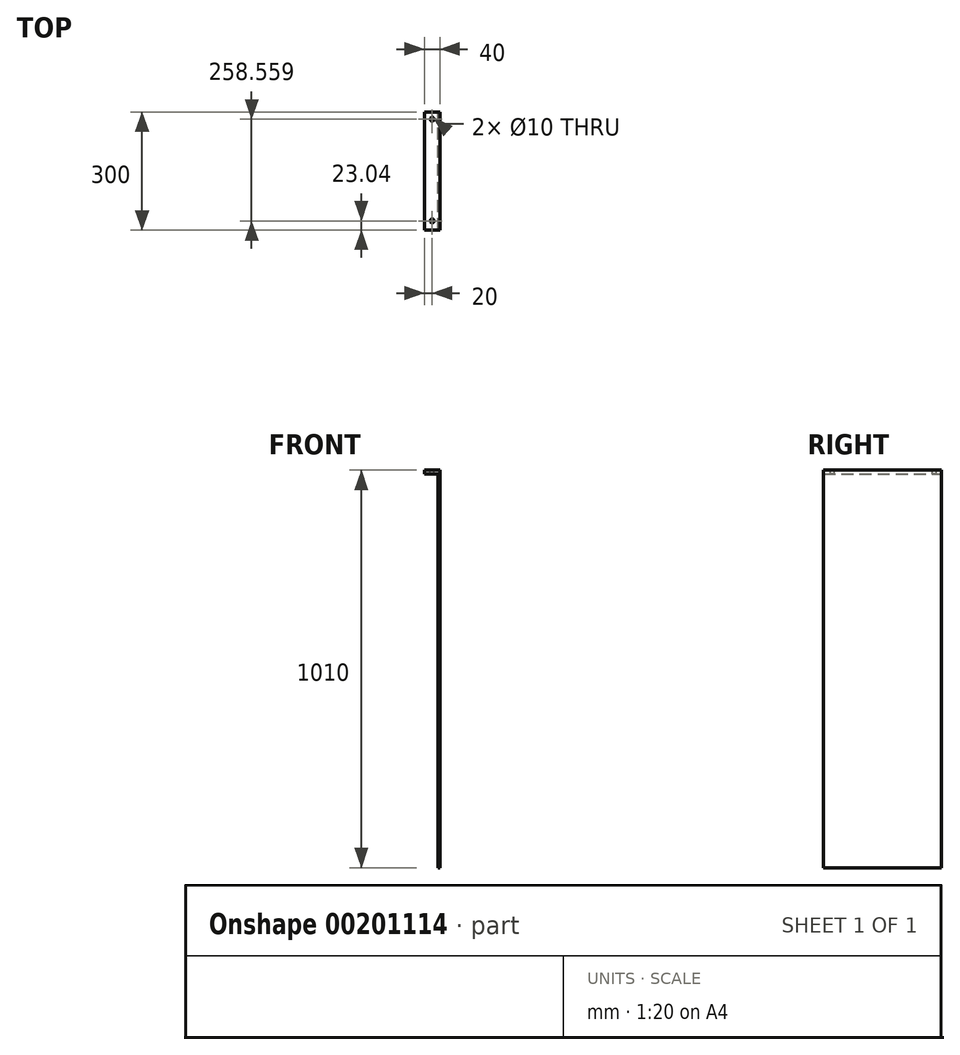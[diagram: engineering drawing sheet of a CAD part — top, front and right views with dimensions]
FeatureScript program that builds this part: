
annotation { "Feature Type Name" : "Feature", "Feature Type Description" : "" }
export const myFeature = defineFeature(function(context is Context, id is Id, definition is map)
    precondition{}
    {
        {
            var Q0;
            Q0=qCreatedBy(makeId("Top.planeOp"),FACE);
            var sketch = newSketch(context, id + "F0", { "sketchPlane" : qUnion([Q0])});
            skLineSegment(sketch, "E0.bottom", {"start": v(20, -150) * mm, "end": v(-20, -150) * mm});
            skLineSegment(sketch, "E0.top", {"start": v(20, 150) * mm, "end": v(-20, 150) * mm});
            skLineSegment(sketch, "E0.left", {"start": v(20, -150) * mm, "end": v(20, 150) * mm});
            skLineSegment(sketch, "E0.right", {"start": v(-20, -150) * mm, "end": v(-20, 150) * mm});
            skPoint(sketch, "E0.middle", {"position": v(0, 0) * mm});
            skCircle(sketch, "E1", {"center": v(0, -126.96) * mm, "radius": 5 * mm});
            skCircle(sketch, "E2", {"center": v(0, 131.6) * mm, "radius": 5 * mm});
            skSolve(sketch);
        }
        {
            var Q0;
            Q0 = qSketchRegion(id + "F0", true);
            extrude(context, id + "F1", {"entities" : qUnion([Q0]), "oppositeDirection" : true, "depth" : 10 * mm});
        }
        {
            var Q0;
            Q0=makeQuery(id+"F1.opExtrude","CAP_FACE",FACE,{"disambiguationData":[OSD([sQuery(id+"F0.wireOp",EDGE,"E0.bottom"),sQuery(id+"F0.wireOp",EDGE,"E0.top"),sQuery(id+"F0.wireOp",EDGE,"E0.left"),sQuery(id+"F0.wireOp",EDGE,"E0.right"),sQuery(id+"F0.wireOp",EDGE,"E1"),sQuery(id+"F0.wireOp",EDGE,"E2")])],"isStart":false});
            var sketch = newSketch(context, id + "F2", { "sketchPlane" : qUnion([Q0])});
            skLineSegment(sketch, "E3.bottom", {"start": v(20, 150) * mm, "end": v(14.55, 150) * mm});
            skLineSegment(sketch, "E3.top", {"start": v(20, -150) * mm, "end": v(14.55, -150) * mm});
            skLineSegment(sketch, "E3.left", {"start": v(20, 150) * mm, "end": v(20, -150) * mm});
            skLineSegment(sketch, "E3.right", {"start": v(14.55, 150) * mm, "end": v(14.55, -150) * mm});
            skSolve(sketch);
        }
        {
            var Q0;
            Q0 = qSketchRegion(id + "F2", true);
            extrude(context, id + "F3", {"entities" : qUnion([Q0]), "operationType" : NewBodyOperationType.ADD, "depth" : 1000 * mm});
        }
    });
